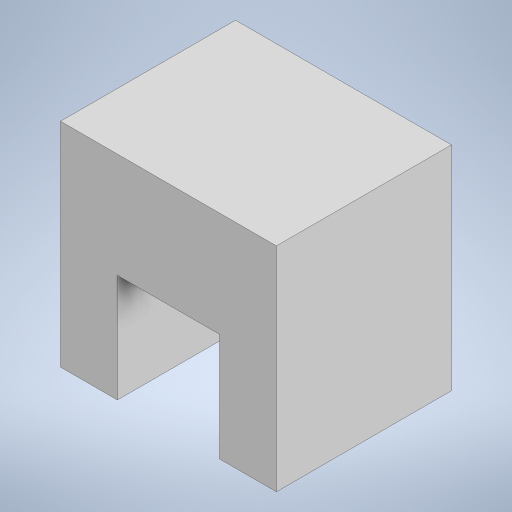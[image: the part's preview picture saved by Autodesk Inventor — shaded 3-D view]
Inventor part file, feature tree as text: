
AUTODESK INVENTOR PART (.ipt)
format: ipt  version: 2024.3 (Build 283343000, 343)  size: 213,504 bytes
history: native  units: mm
features: extrude x2, sketch x1
ambient origin geometry x8: Origin, YZ Plane, XZ Plane, XY Plane, X Axis, Y Axis, Z Axis, Center Point
bodies: Solid1 (feature_tree)
feature tree (3):
  sketch  "Sketch1"  dims[d0=7.4mm d1=7.3mm d2=3.5mm d3=3.7mm d4=6.0mm d5=0.0mm d6=2.0mm d7=0.0mm]
  extrude  "Extrusion1"  Depth=7.3mm
  extrude  "Extrusion2"  Depth=3.5mm
